# Revit family: CUEE
name_source: partatom
category: Lighting Fixtures
revit_build: Autodesk Revit 2014 (Build: 20130308_1515(x64)
units: mm (PartAtom-declared; Revit-internal decimal feet)

## types (1)
- CUEE-218-BI
    Apparent Load = 40 VA
    Assembly Code = D5020200
    Color Filter = 16777215
    Connector Description = Lighting Connector
    Default Elevation = 1219.2 mm  [stored 4 ft]
    Description = The Curie Elite is a recessed fluorescent specifically designed for use in solid or modular ceiling types. The luminaire is SOLAS B15 approved and suitable for use in offshore accommodation modules for both task and emergency lighting. The body is made from zinc coated sheet steel and the diffuser from prismatic polycarbonate with textured side facing down. Where it meets the ceiling apeture the body is fitted with a flipper seal providing excellent sealing against surface irregularities. The range is flexible to allow luminaires to be recessed into either plasterboard and modular (600x600mm & 600x1200mm) ceiling types.
    Dimming Lamp Color Temperature Shift = <None>
    Drum-Height = 609.6 mm  [stored 2 ft]
    Emit Shape Visible in Rendering = No
    Emit from Rectangle Length = 624 mm  [stored 2.04724 ft]
    Emit from Rectangle Width = 624 mm  [stored 2.04724 ft]
    Features = B15 SOLAS fire rating - appropriate
insulation is required over the luminaire
Battery management monitoring
& automatic self test
Simple and easy access via front cover for
lamp replacement and maintenance
Suspended gear tray for ease
of maintenance
Automatic lamp
de-energisation on opening
Electronic control gear gives 50/60Hz
operation, high power factor correction
and regulation of lamp output
dc operation (non emergency)
Local switching arrangement
as standard
End of life (EOL) protection
to IEC 60079-7
(with EOL I and EOL II functionality)
    Fixture distribution = Direct
    Housing Material = Paint - Hubbell - Matte White
    IP Rating = IP65
    Lamp = LED
    Length = 624 mm  [stored 2.04724 ft]
    Load Classification = Lighting
    Manufacturer = Chalmit
    Model = CUEE-218-BI
    Mounting = Paint - Hubbell - Light Silver
    Photometric Web File = CHL_CUEE_218_BI.ies
    Power Factor = 1
    Product Documentation Link = https://hubbellcdn.com
    Product Link = https://www.hubbell.com
    Reflector Finish = Hubbell - White Glass
    Tilt Angle = 90.00°
    URL = https://www.hubbell.com
    Voltage = 120 V
    Warranty = 5 years Warranty
    Wattage Comments = 40W
    Watts = 40 W
    Width = 624 mm  [stored 2.04724 ft]
    Wings = Paint - Hubbell - Light Silver

note: [stored X ft] marks values corroborated as IEEE doubles in the binary element streams (Revit-internal decimal feet)

## geometry (parser evidence)
native form markers: Sweep x4
no freeform markers — native parametric forms only
